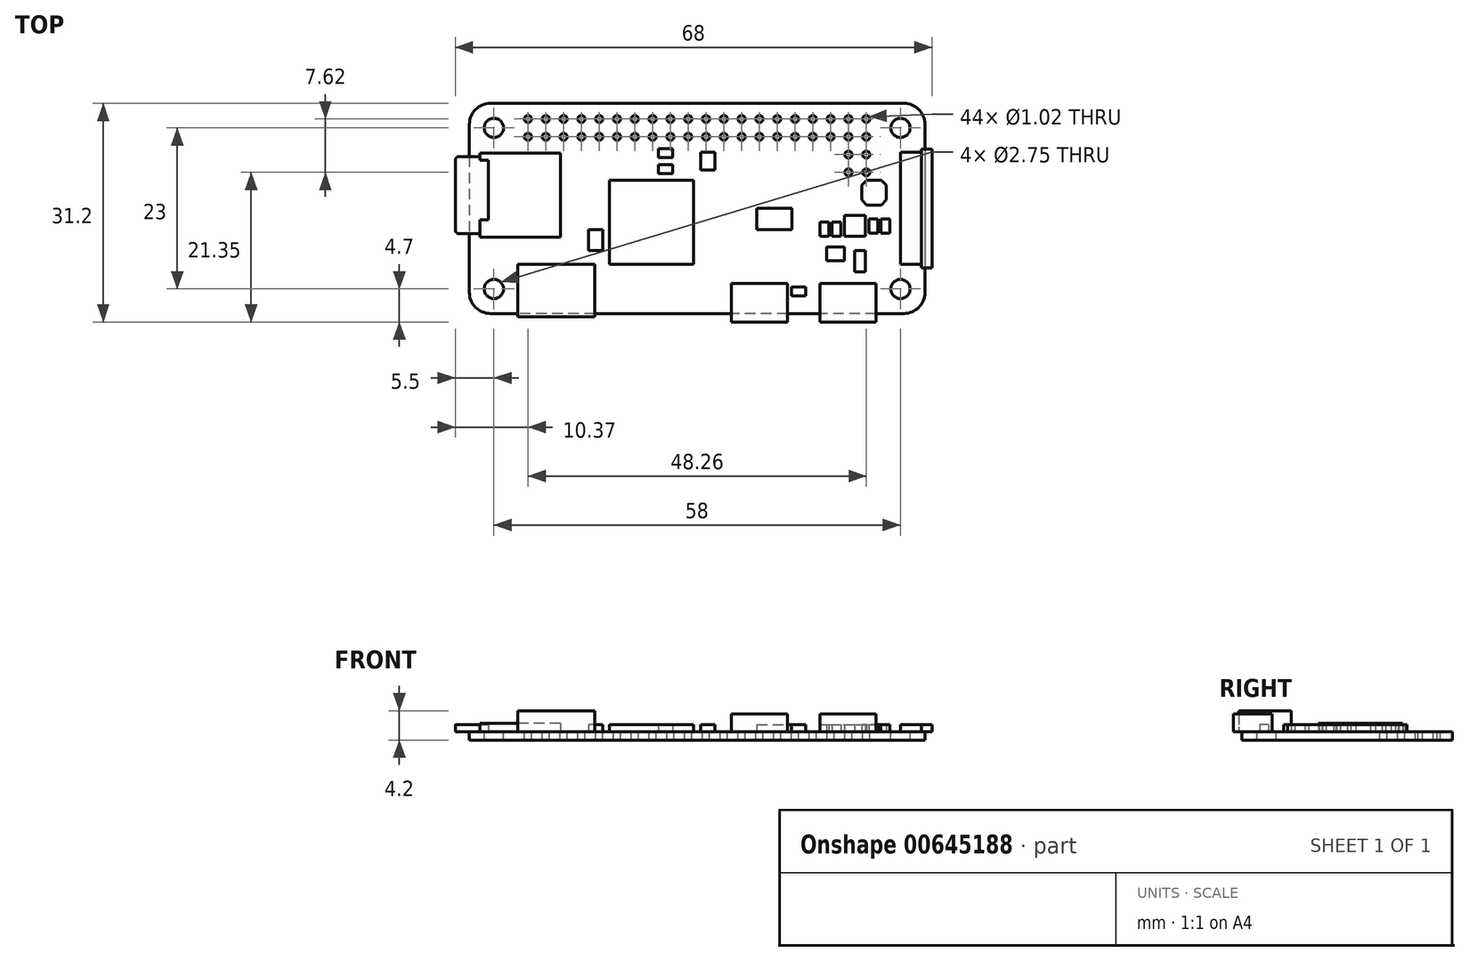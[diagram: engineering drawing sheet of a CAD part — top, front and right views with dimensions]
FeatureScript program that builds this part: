
annotation { "Feature Type Name" : "Feature", "Feature Type Description" : "" }
export const myFeature = defineFeature(function(context is Context, id is Id, definition is map)
    precondition{}
    {
        {
            var Q0;
            Q0=qCreatedBy(makeId("Top.planeOp"),FACE);
            var sketch = newSketch(context, id + "F0", { "sketchPlane" : qUnion([Q0])});
            skLineSegment(sketch, "E0.bottom", {"start": v(29.5, 15) * mm, "end": v(-29.5, 15) * mm});
            skLineSegment(sketch, "E0.top", {"start": v(29.5, -15) * mm, "end": v(-29.5, -15) * mm});
            skLineSegment(sketch, "E0.left", {"start": v(32.5, 12) * mm, "end": v(32.5, -12) * mm});
            skLineSegment(sketch, "E0.right", {"start": v(-32.5, 12) * mm, "end": v(-32.5, -12) * mm});
            skPoint(sketch, "E0.middle", {"position": v(0, 0) * mm});
            skPoint(sketch, "E1.visualSharp", {"position": v(-32.5, 15) * mm});
            skArc(sketch, "E1.filletArc", {"start": v(-29.5, 15) * mm, "mid": v(-31.62, 14.12) * mm, "end": v(-32.5, 12) * mm});
            skPoint(sketch, "E2.visualSharp", {"position": v(32.5, 15) * mm});
            skArc(sketch, "E2.filletArc", {"start": v(32.5, 12) * mm, "mid": v(31.62, 14.12) * mm, "end": v(29.5, 15) * mm});
            skPoint(sketch, "E3.visualSharp", {"position": v(32.5, -15) * mm});
            skArc(sketch, "E3.filletArc", {"start": v(29.5, -15) * mm, "mid": v(31.62, -14.12) * mm, "end": v(32.5, -12) * mm});
            skPoint(sketch, "E4.visualSharp", {"position": v(-32.5, -15) * mm});
            skArc(sketch, "E4.filletArc", {"start": v(-32.5, -12) * mm, "mid": v(-31.62, -14.12) * mm, "end": v(-29.5, -15) * mm});
            skLineSegment(sketch, "E5.bottom", {"start": v(29, 11.5) * mm, "end": v(-29, 11.5) * mm, "construction": true});
            skLineSegment(sketch, "E5.top", {"start": v(29, -11.5) * mm, "end": v(-29, -11.5) * mm, "construction": true});
            skLineSegment(sketch, "E5.left", {"start": v(29, 11.5) * mm, "end": v(29, -11.5) * mm, "construction": true});
            skLineSegment(sketch, "E5.right", {"start": v(-29, 11.5) * mm, "end": v(-29, -11.5) * mm, "construction": true});
            skCircle(sketch, "E6", {"center": v(29, 11.5) * mm, "radius": 3 * mm});
            skCircle(sketch, "E7", {"center": v(29, 11.5) * mm, "radius": 1.38 * mm});
            skCircle(sketch, "E8", {"center": v(-29, 11.5) * mm, "radius": 1.38 * mm});
            skCircle(sketch, "E9", {"center": v(-29, 11.5) * mm, "radius": 3 * mm});
            skCircle(sketch, "E10", {"center": v(-29, -11.5) * mm, "radius": 3 * mm});
            skCircle(sketch, "E11", {"center": v(-29, -11.5) * mm, "radius": 1.38 * mm});
            skCircle(sketch, "E12", {"center": v(29, -11.5) * mm, "radius": 1.38 * mm});
            skCircle(sketch, "E13", {"center": v(29, -11.5) * mm, "radius": 3 * mm});
            skCircle(sketch, "E14", {"center": v(24.13, 12.77) * mm, "radius": 0.5 * mm});
            skCircle(sketch, "E15", {"center": v(24.13, 10.23) * mm, "radius": 0.5 * mm});
            skLineSegment(sketch, "E16", {"start": v(24.13, 12.77) * mm, "end": v(24.13, 10.23) * mm, "construction": true});
            skPoint(sketch, "E17", {"position": v(24.13, 11.5) * mm});
            skCircle(sketch, "E18.1.0.0", {"center": v(21.59, 12.77) * mm, "radius": 0.5 * mm});
            skCircle(sketch, "E18.1.0.1", {"center": v(21.59, 10.23) * mm, "radius": 0.5 * mm});
            skCircle(sketch, "E18.2.0.0", {"center": v(19.05, 12.77) * mm, "radius": 0.5 * mm});
            skCircle(sketch, "E18.2.0.1", {"center": v(19.05, 10.23) * mm, "radius": 0.5 * mm});
            skCircle(sketch, "E18.3.0.0", {"center": v(16.5, 12.77) * mm, "radius": 0.5 * mm});
            skCircle(sketch, "E18.3.0.1", {"center": v(16.5, 10.23) * mm, "radius": 0.5 * mm});
            skCircle(sketch, "E18.4.0.0", {"center": v(13.97, 12.77) * mm, "radius": 0.5 * mm});
            skCircle(sketch, "E18.4.0.1", {"center": v(13.97, 10.23) * mm, "radius": 0.5 * mm});
            skCircle(sketch, "E18.5.0.0", {"center": v(11.43, 12.77) * mm, "radius": 0.5 * mm});
            skCircle(sketch, "E18.5.0.1", {"center": v(11.43, 10.23) * mm, "radius": 0.5 * mm});
            skCircle(sketch, "E18.6.0.0", {"center": v(8.89, 12.77) * mm, "radius": 0.5 * mm});
            skCircle(sketch, "E18.6.0.1", {"center": v(8.89, 10.23) * mm, "radius": 0.5 * mm});
            skCircle(sketch, "E18.7.0.0", {"center": v(6.35, 12.77) * mm, "radius": 0.5 * mm});
            skCircle(sketch, "E18.7.0.1", {"center": v(6.35, 10.23) * mm, "radius": 0.5 * mm});
            skCircle(sketch, "E18.8.0.0", {"center": v(3.8, 12.77) * mm, "radius": 0.5 * mm});
            skCircle(sketch, "E18.8.0.1", {"center": v(3.8, 10.23) * mm, "radius": 0.5 * mm});
            skCircle(sketch, "E18.9.0.0", {"center": v(1.27, 12.77) * mm, "radius": 0.5 * mm});
            skCircle(sketch, "E18.9.0.1", {"center": v(1.27, 10.23) * mm, "radius": 0.5 * mm});
            skCircle(sketch, "E18.10.0.0", {"center": v(-1.27, 12.77) * mm, "radius": 0.5 * mm});
            skCircle(sketch, "E18.10.0.1", {"center": v(-1.27, 10.23) * mm, "radius": 0.5 * mm});
            skCircle(sketch, "E18.11.0.0", {"center": v(-3.81, 12.77) * mm, "radius": 0.5 * mm});
            skCircle(sketch, "E18.11.0.1", {"center": v(-3.81, 10.23) * mm, "radius": 0.5 * mm});
            skCircle(sketch, "E18.12.0.0", {"center": v(-6.35, 12.77) * mm, "radius": 0.5 * mm});
            skCircle(sketch, "E18.12.0.1", {"center": v(-6.35, 10.23) * mm, "radius": 0.5 * mm});
            skCircle(sketch, "E18.13.0.0", {"center": v(-8.9, 12.77) * mm, "radius": 0.5 * mm});
            skCircle(sketch, "E18.13.0.1", {"center": v(-8.9, 10.23) * mm, "radius": 0.5 * mm});
            skCircle(sketch, "E18.14.0.0", {"center": v(-11.43, 12.77) * mm, "radius": 0.5 * mm});
            skCircle(sketch, "E18.14.0.1", {"center": v(-11.43, 10.23) * mm, "radius": 0.5 * mm});
            skCircle(sketch, "E18.15.0.0", {"center": v(-13.97, 12.77) * mm, "radius": 0.5 * mm});
            skCircle(sketch, "E18.15.0.1", {"center": v(-13.97, 10.23) * mm, "radius": 0.5 * mm});
            skCircle(sketch, "E18.16.0.0", {"center": v(-16.51, 12.77) * mm, "radius": 0.5 * mm});
            skCircle(sketch, "E18.16.0.1", {"center": v(-16.51, 10.23) * mm, "radius": 0.5 * mm});
            skCircle(sketch, "E18.17.0.0", {"center": v(-19.05, 12.77) * mm, "radius": 0.5 * mm});
            skCircle(sketch, "E18.17.0.1", {"center": v(-19.05, 10.23) * mm, "radius": 0.5 * mm});
            skCircle(sketch, "E18.18.0.0", {"center": v(-21.6, 12.77) * mm, "radius": 0.5 * mm});
            skCircle(sketch, "E18.18.0.1", {"center": v(-21.6, 10.23) * mm, "radius": 0.5 * mm});
            skCircle(sketch, "E18.19.0.0", {"center": v(-24.13, 12.77) * mm, "radius": 0.5 * mm});
            skCircle(sketch, "E18.19.0.1", {"center": v(-24.13, 10.23) * mm, "radius": 0.5 * mm});
            skLineSegment(sketch, "E18.direction1", {"start": v(24.13, 12.77) * mm, "end": v(21.59, 12.77) * mm, "construction": true});
            skCircle(sketch, "E19.1.0.0", {"center": v(21.59, 7.69) * mm, "radius": 0.5 * mm});
            skCircle(sketch, "E19.1.0.1", {"center": v(24.13, 7.69) * mm, "radius": 0.5 * mm});
            skCircle(sketch, "E19.1.0.2", {"center": v(24.13, 5.15) * mm, "radius": 0.5 * mm});
            skCircle(sketch, "E19.1.0.3", {"center": v(21.59, 5.15) * mm, "radius": 0.5 * mm});
            skLineSegment(sketch, "E19.direction1", {"start": v(21.59, 12.77) * mm, "end": v(21.59, 7.69) * mm, "construction": true});
            skSolve(sketch);
        }
        {
            var Q0;
            Q0=qCreatedBy(makeId("Top.planeOp"),FACE);
            var sketch = newSketch(context, id + "F1", { "sketchPlane" : qUnion([Q0])});
            skLineSegment(sketch, "E20.bottom", {"start": v(33.5, -8.5) * mm, "end": v(32, -8.5) * mm});
            skLineSegment(sketch, "E20.top", {"start": v(33.5, 8.5) * mm, "end": v(32, 8.5) * mm});
            skLineSegment(sketch, "E20.left", {"start": v(33.5, -8.5) * mm, "end": v(33.5, 8.5) * mm});
            skLineSegment(sketch, "E20.right", {"start": v(32, -8.5) * mm, "end": v(32, 8.5) * mm});
            skPoint(sketch, "E20.middle", {"position": v(32.75, 0) * mm});
            skLineSegment(sketch, "E21.bottom", {"start": v(-14.6, -15.5) * mm, "end": v(-25.6, -15.5) * mm});
            skLineSegment(sketch, "E21.top", {"start": v(-14.6, -8) * mm, "end": v(-25.6, -8) * mm});
            skLineSegment(sketch, "E21.left", {"start": v(-14.6, -15.5) * mm, "end": v(-14.6, -8) * mm});
            skLineSegment(sketch, "E21.right", {"start": v(-25.6, -15.5) * mm, "end": v(-25.6, -8) * mm});
            skPoint(sketch, "E21.middle", {"position": v(-20.1, -11.75) * mm});
            skLineSegment(sketch, "E22.bottom", {"start": v(12.9, -16.2) * mm, "end": v(4.9, -16.2) * mm});
            skLineSegment(sketch, "E22.top", {"start": v(12.9, -10.7) * mm, "end": v(4.9, -10.7) * mm});
            skLineSegment(sketch, "E22.left", {"start": v(12.9, -16.2) * mm, "end": v(12.9, -10.7) * mm});
            skLineSegment(sketch, "E22.right", {"start": v(4.9, -16.2) * mm, "end": v(4.9, -10.7) * mm});
            skPoint(sketch, "E22.middle", {"position": v(8.9, -13.45) * mm});
            skLineSegment(sketch, "E23.bottom", {"start": v(25.5, -16.2) * mm, "end": v(17.5, -16.2) * mm});
            skLineSegment(sketch, "E23.top", {"start": v(25.5, -10.7) * mm, "end": v(17.5, -10.7) * mm});
            skLineSegment(sketch, "E23.left", {"start": v(25.5, -16.2) * mm, "end": v(25.5, -10.7) * mm});
            skLineSegment(sketch, "E23.right", {"start": v(17.5, -16.2) * mm, "end": v(17.5, -10.7) * mm});
            skPoint(sketch, "E23.middle", {"position": v(21.5, -13.45) * mm});
            skLineSegment(sketch, "E24.bottom", {"start": v(-19.5, 7.9) * mm, "end": v(-31, 7.9) * mm});
            skLineSegment(sketch, "E24.top", {"start": v(-19.5, -4.1) * mm, "end": v(-31, -4.1) * mm});
            skLineSegment(sketch, "E24.left", {"start": v(-19.5, 7.9) * mm, "end": v(-19.5, -4.1) * mm});
            skLineSegment(sketch, "E24.right", {"start": v(-31, 7.9) * mm, "end": v(-31, -4.1) * mm});
            skPoint(sketch, "E24.middle", {"position": v(-25.25, 1.9) * mm});
            skLineSegment(sketch, "E25", {"start": v(-31, 7.4) * mm, "end": v(-34, 7.4) * mm});
            skLineSegment(sketch, "E26", {"start": v(-34.5, 6.9) * mm, "end": v(-34.5, -3.1) * mm});
            skLineSegment(sketch, "E27", {"start": v(-34, -3.6) * mm, "end": v(-31, -3.6) * mm});
            skPoint(sketch, "E28.visualSharp", {"position": v(-34.5, 7.4) * mm});
            skArc(sketch, "E28.filletArc", {"start": v(-34, 7.4) * mm, "mid": v(-34.35, 7.25) * mm, "end": v(-34.5, 6.9) * mm});
            skPoint(sketch, "E29.visualSharp", {"position": v(-34.5, -3.6) * mm});
            skArc(sketch, "E29.filletArc", {"start": v(-34.5, -3.1) * mm, "mid": v(-34.35, -3.45) * mm, "end": v(-34, -3.6) * mm});
            skPoint(sketch, "E30", {"position": v(-34.5, 1.9) * mm});
            skLineSegment(sketch, "E31", {"start": v(-31, 6.9) * mm, "end": v(-29.8, 6.9) * mm});
            skLineSegment(sketch, "E32", {"start": v(-29.8, 6.9) * mm, "end": v(-29.8, -1.6) * mm});
            skLineSegment(sketch, "E33", {"start": v(-29.8, -1.6) * mm, "end": v(-31, -1.6) * mm});
            skLineSegment(sketch, "E34", {"start": v(32, 8) * mm, "end": v(29, 8) * mm});
            skLineSegment(sketch, "E35", {"start": v(29, 8) * mm, "end": v(29, -8) * mm});
            skLineSegment(sketch, "E36", {"start": v(29, -8) * mm, "end": v(32, -8) * mm});
            skLineSegment(sketch, "E37", {"start": v(32.75, 0) * mm, "end": v(29, 0) * mm, "construction": true});
            skSolve(sketch);
        }
        {
            var Q0;
            Q0=qCreatedBy(makeId("Top.planeOp"),FACE);
            var sketch = newSketch(context, id + "F2", { "sketchPlane" : qUnion([Q0])});
            skLineSegment(sketch, "E38.bottom", {"start": v(-12.5, -8) * mm, "end": v(-0.5, -8) * mm});
            skLineSegment(sketch, "E38.top", {"start": v(-12.5, 4) * mm, "end": v(-0.5, 4) * mm});
            skLineSegment(sketch, "E38.left", {"start": v(-12.5, -8) * mm, "end": v(-12.5, 4) * mm});
            skLineSegment(sketch, "E38.right", {"start": v(-0.5, -8) * mm, "end": v(-0.5, 4) * mm});
            skLineSegment(sketch, "E39.bottom", {"start": v(-5.53, 8.54) * mm, "end": v(-3.5, 8.54) * mm});
            skLineSegment(sketch, "E39.top", {"start": v(-5.53, 7.27) * mm, "end": v(-3.5, 7.27) * mm});
            skLineSegment(sketch, "E39.left", {"start": v(-5.53, 8.54) * mm, "end": v(-5.53, 7.27) * mm});
            skLineSegment(sketch, "E39.right", {"start": v(-3.5, 8.54) * mm, "end": v(-3.5, 7.27) * mm});
            skLineSegment(sketch, "E40.bottom", {"start": v(-5.53, 6.27) * mm, "end": v(-3.5, 6.27) * mm});
            skLineSegment(sketch, "E40.top", {"start": v(-5.53, 5) * mm, "end": v(-3.5, 5) * mm});
            skLineSegment(sketch, "E40.left", {"start": v(-5.53, 6.27) * mm, "end": v(-5.53, 5) * mm});
            skLineSegment(sketch, "E40.right", {"start": v(-3.5, 6.27) * mm, "end": v(-3.5, 5) * mm});
            skLineSegment(sketch, "E41.bottom", {"start": v(13.47, -11.23) * mm, "end": v(15.5, -11.23) * mm});
            skLineSegment(sketch, "E41.top", {"start": v(13.47, -12.5) * mm, "end": v(15.5, -12.5) * mm});
            skLineSegment(sketch, "E41.left", {"start": v(13.47, -11.23) * mm, "end": v(13.47, -12.5) * mm});
            skLineSegment(sketch, "E41.right", {"start": v(15.5, -11.23) * mm, "end": v(15.5, -12.5) * mm});
            skLineSegment(sketch, "E42.bottom", {"start": v(17.5, -1.97) * mm, "end": v(18.77, -1.97) * mm});
            skLineSegment(sketch, "E42.top", {"start": v(17.5, -4) * mm, "end": v(18.77, -4) * mm});
            skLineSegment(sketch, "E42.left", {"start": v(17.5, -1.97) * mm, "end": v(17.5, -4) * mm});
            skLineSegment(sketch, "E42.right", {"start": v(18.77, -1.97) * mm, "end": v(18.77, -4) * mm});
            skLineSegment(sketch, "E43.bottom", {"start": v(19.25, -1.97) * mm, "end": v(20.52, -1.97) * mm});
            skLineSegment(sketch, "E43.top", {"start": v(19.25, -4) * mm, "end": v(20.52, -4) * mm});
            skLineSegment(sketch, "E43.left", {"start": v(19.25, -1.97) * mm, "end": v(19.25, -4) * mm});
            skLineSegment(sketch, "E43.right", {"start": v(20.52, -1.97) * mm, "end": v(20.52, -4) * mm});
            skLineSegment(sketch, "E44.bottom", {"start": v(24.48, -1.48) * mm, "end": v(25.75, -1.48) * mm});
            skLineSegment(sketch, "E44.top", {"start": v(24.48, -3.52) * mm, "end": v(25.75, -3.52) * mm});
            skLineSegment(sketch, "E44.left", {"start": v(24.48, -1.48) * mm, "end": v(24.48, -3.52) * mm});
            skLineSegment(sketch, "E44.right", {"start": v(25.75, -1.48) * mm, "end": v(25.75, -3.52) * mm});
            skLineSegment(sketch, "E45.bottom", {"start": v(26.23, -1.48) * mm, "end": v(27.5, -1.48) * mm});
            skLineSegment(sketch, "E45.top", {"start": v(26.23, -3.52) * mm, "end": v(27.5, -3.52) * mm});
            skLineSegment(sketch, "E45.left", {"start": v(26.23, -1.48) * mm, "end": v(26.23, -3.52) * mm});
            skLineSegment(sketch, "E45.right", {"start": v(27.5, -1.48) * mm, "end": v(27.5, -3.52) * mm});
            skLineSegment(sketch, "E46.bottom", {"start": v(-13.5, -3) * mm, "end": v(-15.5, -3) * mm});
            skLineSegment(sketch, "E46.top", {"start": v(-13.5, -6) * mm, "end": v(-15.5, -6) * mm});
            skLineSegment(sketch, "E46.left", {"start": v(-13.5, -3) * mm, "end": v(-13.5, -6) * mm});
            skLineSegment(sketch, "E46.right", {"start": v(-15.5, -3) * mm, "end": v(-15.5, -6) * mm});
            skLineSegment(sketch, "E47.bottom", {"start": v(8.5, 0) * mm, "end": v(13.5, 0) * mm});
            skLineSegment(sketch, "E47.top", {"start": v(8.5, -3) * mm, "end": v(13.5, -3) * mm});
            skLineSegment(sketch, "E47.left", {"start": v(8.5, 0) * mm, "end": v(8.5, -3) * mm});
            skLineSegment(sketch, "E47.right", {"start": v(13.5, 0) * mm, "end": v(13.5, -3) * mm});
            skLineSegment(sketch, "E48.bottom", {"start": v(21, -1) * mm, "end": v(24, -1) * mm});
            skLineSegment(sketch, "E48.top", {"start": v(21, -4) * mm, "end": v(24, -4) * mm});
            skLineSegment(sketch, "E48.left", {"start": v(21, -1) * mm, "end": v(21, -4) * mm});
            skLineSegment(sketch, "E48.right", {"start": v(24, -1) * mm, "end": v(24, -4) * mm});
            skLineSegment(sketch, "E49.bottom", {"start": v(0.5, 8) * mm, "end": v(2.5, 8) * mm});
            skLineSegment(sketch, "E49.top", {"start": v(0.5, 5.5) * mm, "end": v(2.5, 5.5) * mm});
            skLineSegment(sketch, "E49.left", {"start": v(0.5, 8) * mm, "end": v(0.5, 5.5) * mm});
            skLineSegment(sketch, "E49.right", {"start": v(2.5, 8) * mm, "end": v(2.5, 5.5) * mm});
            skLineSegment(sketch, "E50.bottom", {"start": v(18.5, -5.5) * mm, "end": v(21, -5.5) * mm});
            skLineSegment(sketch, "E50.top", {"start": v(18.5, -7.5) * mm, "end": v(21, -7.5) * mm});
            skLineSegment(sketch, "E50.left", {"start": v(18.5, -5.5) * mm, "end": v(18.5, -7.5) * mm});
            skLineSegment(sketch, "E50.right", {"start": v(21, -5.5) * mm, "end": v(21, -7.5) * mm});
            skLineSegment(sketch, "E51.bottom", {"start": v(22.48, -6) * mm, "end": v(24, -6) * mm});
            skLineSegment(sketch, "E51.top", {"start": v(22.48, -9.05) * mm, "end": v(24, -9.05) * mm});
            skLineSegment(sketch, "E51.left", {"start": v(22.48, -6) * mm, "end": v(22.48, -9.05) * mm});
            skLineSegment(sketch, "E51.right", {"start": v(24, -6) * mm, "end": v(24, -9.05) * mm});
            skLineSegment(sketch, "E52", {"start": v(24, -2.5) * mm, "end": v(24.48, -2.5) * mm, "construction": true});
            skLineSegment(sketch, "E53", {"start": v(26.23, -3.52) * mm, "end": v(25.75, -3.52) * mm, "construction": true});
            skLineSegment(sketch, "E54", {"start": v(21, -4) * mm, "end": v(20.52, -4) * mm, "construction": true});
            skLineSegment(sketch, "E55", {"start": v(19.25, -4) * mm, "end": v(18.77, -4) * mm, "construction": true});
            skLineSegment(sketch, "E56", {"start": v(23.5, 3.3) * mm, "end": v(23.5, 1.2) * mm});
            skLineSegment(sketch, "E57", {"start": v(23.5, 1.2) * mm, "end": v(24.2, 0.5) * mm});
            skLineSegment(sketch, "E58", {"start": v(24.2, 0.5) * mm, "end": v(26.3, 0.5) * mm});
            skLineSegment(sketch, "E59", {"start": v(26.3, 0.5) * mm, "end": v(27, 1.2) * mm});
            skLineSegment(sketch, "E60", {"start": v(27, 1.2) * mm, "end": v(27, 3.3) * mm});
            skLineSegment(sketch, "E61", {"start": v(27, 3.3) * mm, "end": v(26.3, 4) * mm});
            skLineSegment(sketch, "E62", {"start": v(26.3, 4) * mm, "end": v(24.2, 4) * mm});
            skLineSegment(sketch, "E63", {"start": v(24.2, 4) * mm, "end": v(23.5, 3.3) * mm});
            skSolve(sketch);
        }
        {
            var Q0;
            Q0=qSketchRegion(id+"F0",true);
            var Q1;
            Q1=makeQuery(id+"F0.imprint","IMPRINT",FACE,{"disambiguationData":[TD([[makeQuery(id+"F0.imprint","IMPRINT",EDGE,{"derivedFrom":sQuery(id+"F0.wireOp",EDGE,"E10")}),1.0]])]});
            var Q2;
            Q2=makeQuery(id+"F0.imprint","IMPRINT",FACE,{"disambiguationData":[TD([[makeQuery(id+"F0.imprint","IMPRINT",EDGE,{"derivedFrom":sQuery(id+"F0.wireOp",EDGE,"E8")}),-1.0]])]});
            var Q3;
            Q3=makeQuery(id+"F0.imprint","IMPRINT",FACE,{"disambiguationData":[TD([[makeQuery(id+"F0.imprint","IMPRINT",EDGE,{"derivedFrom":sQuery(id+"F0.wireOp",EDGE,"E6")}),1.0]])]});
            var Q4;
            Q4=makeQuery(id+"F0.imprint","IMPRINT",FACE,{"disambiguationData":[TD([[makeQuery(id+"F0.imprint","IMPRINT",EDGE,{"derivedFrom":sQuery(id+"F0.wireOp",EDGE,"E12")}),-1.0]])]});
            extrude(context, id + "F3", {"entities" : qUnion([Q0, Q1, Q2, Q3, Q4]), "oppositeDirection" : true, "depth" : 1.2 * mm, "offsetDistance" : 25 * mm});
        }
        {
            var Q0;
            Q0=makeQuery(id+"F1.imprint","IMPRINT",FACE,{"disambiguationData":[TD([[makeQuery(id+"F1.imprint","IMPRINT",EDGE,{"derivedFrom":sQuery(id+"F1.wireOp",EDGE,"E20.bottom")}),-1.0]])]});
            extrude(context, id + "F4", {"entities" : qUnion([Q0]), "depth" : 1 * mm, "offsetDistance" : 25 * mm});
        }
        {
            var Q0;
            {var subQ0=sQuery(id+"F1.wireOp",EDGE,"E34");Q0=makeQuery(id+"F1.imprint","IMPRINT",FACE,{"disambiguationData":[TD([[makeQuery(id+"F1.imprint","IMPRINT",EDGE,{"derivedFrom":subQ0}),1.0]])]});}
            extrude(context, id + "F5", {"entities" : qUnion([Q0]), "depth" : 1 * mm, "offsetDistance" : 25 * mm});
        }
        {
            var Q0;
            Q0=makeQuery(id+"F1.imprint","IMPRINT",FACE,{"disambiguationData":[TD([[makeQuery(id+"F1.imprint","IMPRINT",EDGE,{"derivedFrom":sQuery(id+"F1.wireOp",EDGE,"E23.bottom")}),-1.0]])]});
            var Q1;
            Q1=makeQuery(id+"F1.imprint","IMPRINT",FACE,{"disambiguationData":[TD([[makeQuery(id+"F1.imprint","IMPRINT",EDGE,{"derivedFrom":sQuery(id+"F1.wireOp",EDGE,"E22.bottom")}),-1.0]])]});
            extrude(context, id + "F6", {"entities" : qUnion([Q0, Q1]), "depth" : 2.5 * mm, "offsetDistance" : 25 * mm});
        }
        {
            var Q0;
            Q0=makeQuery(id+"F1.imprint","IMPRINT",FACE,{"disambiguationData":[TD([[makeQuery(id+"F1.imprint","IMPRINT",EDGE,{"derivedFrom":sQuery(id+"F1.wireOp",EDGE,"E21.bottom")}),-1.0]])]});
            extrude(context, id + "F7", {"entities" : qUnion([Q0]), "depth" : 3 * mm, "offsetDistance" : 25 * mm});
        }
        {
            var Q0;
            {var subQ1=sQuery(id+"F1.wireOp",EDGE,"E24.bottom");Q0=makeQuery(id+"F1.imprint","IMPRINT",FACE,{"disambiguationData":[TD([[makeQuery(id+"F1.imprint","IMPRINT",EDGE,{"derivedFrom":subQ1}),1.0]])]});}
            extrude(context, id + "F8", {"entities" : qUnion([Q0]), "depth" : 1.2 * mm, "offsetDistance" : 25 * mm});
        }
        {
            var Q0;
            {var subQ0=sQuery(id+"F1.wireOp",EDGE,"E31");Q0=makeQuery(id+"F1.imprint","IMPRINT",FACE,{"disambiguationData":[TD([[makeQuery(id+"F1.imprint","IMPRINT",EDGE,{"derivedFrom":subQ0}),-1.0]])]});}
            var Q1;
            {var subQ0=sQuery(id+"F1.wireOp",EDGE,"E25");Q1=makeQuery(id+"F1.imprint","IMPRINT",FACE,{"disambiguationData":[TD([[makeQuery(id+"F1.imprint","IMPRINT",EDGE,{"derivedFrom":subQ0}),1.0]])]});}
            extrude(context, id + "F9", {"entities" : qUnion([Q0, Q1]), "depth" : 1 * mm, "offsetDistance" : 25 * mm});
        }
        {
            var Q0;
            Q0 = qSketchRegion(id + "F2", true);
            extrude(context, id + "F10", {"entities" : qUnion([Q0]), "depth" : 1 * mm, "offsetDistance" : 25 * mm});
        }
    });
